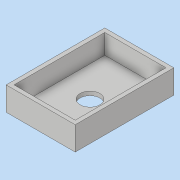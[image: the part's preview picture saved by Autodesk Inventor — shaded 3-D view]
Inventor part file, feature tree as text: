
AUTODESK INVENTOR PART (.ipt)
format: ipt  version: 2019 (Build 230136000, 136)  size: 402,944 bytes
history: native  units: mm
features: sketch x23, extrude x22, projected_geometry x9, other x5, fillet x2, loft x1, shell x1
ambient origin geometry x8: Origin, YZ Plane, XZ Plane, XY Plane, X Axis, Y Axis, Z Axis, Center Point
bodies: Body1 (feature_tree)
feature tree (63):
  other  "хребет2"
  extrude  "Выдавливание115"  Depth=170.0mm
  extrude  "Выдавливание116"  Depth=100.0mm
  extrude  "Выдавливание117"  Depth=17.0mm
  sketch  "Эскиз4"
  other  "РабПлоскость1"
  sketch  "Эскиз5"
  loft  "Лофт1"
  extrude  "Выдавливание2"  Depth=35.0mm
  shell  "Оболочка1"  Thickness=0.0mm
  sketch  "Эскиз21"
  extrude  "Выдавливание16"  TaperAngle=0.0deg  [1 undecoded]
  extrude  "Выдавливание98"  TaperAngle=0.0deg  [1 undecoded]
  extrude  "Выдавливание99"  Depth=130.0mm TaperAngle=0.0deg
  extrude  "Выдавливание100"  Depth=5.0mm
  extrude  "Выдавливание101"  Depth=2.0mm
  extrude  "Выдавливание102"  Depth=2.0mm
  extrude  "Выдавливание103"  Depth=10.0mm TaperAngle=0.0deg
  extrude  "Выдавливание104"  Depth=2.0mm
  extrude  "Выдавливание105"  Depth=37.306mm
  extrude  "Выдавливание106"  Depth=5.0mm
  fillet  "Сопряжение4"  Radius=10.0mm
  extrude  "Выдавливание107"  Depth=38.0mm
  extrude  "Выдавливание108"  Depth=20.0mm
  fillet  "Сопряжение5"  Radius=2.0mm
  other  "РабПлоскость25"
  sketch  "Эскиз125"
  extrude  "Выдавливание109"  Depth=2.0mm
  extrude  "Выдавливание110"  Depth=2.0mm
  extrude  "Выдавливание111"  Depth=10.0mm TaperAngle=0.0deg
  extrude  "Выдавливание112"  Depth=22.206mm
  other  "РабПлоскость26"
  extrude  "Выдавливание113"  Depth=10.0mm TaperAngle=0.0deg
  extrude  "Выдавливание114"  Depth=31.5mm TaperAngle=0.0deg
  sketch  "Эскиз6"
  projected_geometry  "Спроецированная петля1"
  sketch  "Эскиз114"
  sketch  "Эскиз115"
  sketch  "Эскиз116"
  sketch  "Эскиз117"
  sketch  "Эскиз118"
  projected_geometry  "Спроецированная петля45"
  sketch  "Эскиз119"
  sketch  "Эскиз120"
  sketch  "Эскиз121"
  projected_geometry  "Спроецированная петля46"
  sketch  "Эскиз122"
  projected_geometry  "Спроецированная петля47"
  projected_geometry  "Спроецированная петля48"
  sketch  "Эскиз123"
  sketch  "Эскиз124"
  projected_geometry  "Спроецированная петля49"
  projected_geometry  "Спроецированная петля50"
  sketch  "Эскиз126"
  sketch  "Эскиз127"
  projected_geometry  "Спроецированная петля51"
  sketch  "Эскиз128"
  sketch  "Эскиз129"
  sketch  "Эскиз130"
  other  "Твердое тело3"
  sketch  "Эскиз131"
  projected_geometry  "Спроецированная петля52"
  sketch  "Эскиз132"
note: 2 required parameter values undecoded (feature->parameter linkage not recoverable at this tier; creation-order binding heuristic only, values carry confidence <= 0.55)
